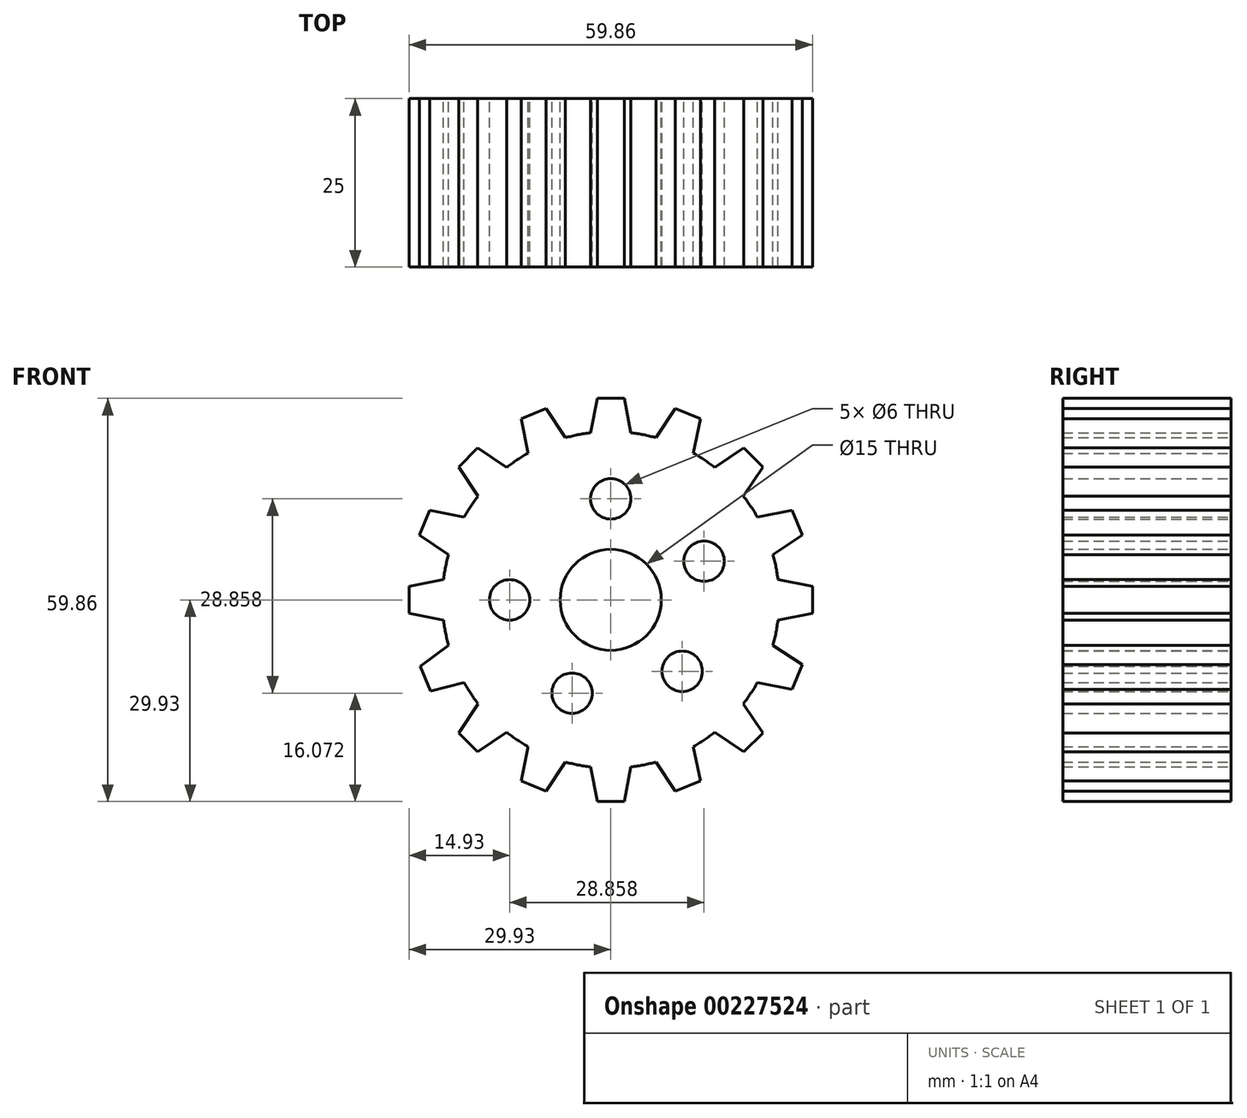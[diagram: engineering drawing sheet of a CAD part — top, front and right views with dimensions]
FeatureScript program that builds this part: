
annotation { "Feature Type Name" : "Feature", "Feature Type Description" : "" }
export const myFeature = defineFeature(function(context is Context, id is Id, definition is map)
    precondition{}
    {
        {
            var Q0;
            Q0=qCreatedBy(makeId("Front.planeOp"),FACE);
            var sketch = newSketch(context, id + "F0", { "sketchPlane" : qUnion([Q0])});
            skCircle(sketch, "E0", {"center": v(0, 0) * mm, "radius": 7.5 * mm});
            skArc(sketch, "E1", {"start": v(6.73, 24.08) * mm, "mid": v(4.88, 24.52) * mm, "end": v(3, 24.82) * mm});
            skLineSegment(sketch, "E2", {"start": v(0, 18) * mm, "end": v(0, 15) * mm, "construction": true});
            skLineSegment(sketch, "E3", {"start": v(-2, 29.93) * mm, "end": v(-3, 24.82) * mm});
            skLineSegment(sketch, "E4", {"start": v(2, 29.93) * mm, "end": v(3, 24.82) * mm});
            skLineSegment(sketch, "E5", {"start": v(-2, 29.93) * mm, "end": v(2, 29.93) * mm});
            skPoint(sketch, "E6", {"position": v(0, 29.93) * mm});
            skLineSegment(sketch, "E7.1.0", {"start": v(-13.3, 26.89) * mm, "end": v(-12.27, 21.78) * mm});
            skLineSegment(sketch, "E7.1.2", {"start": v(-9.6, 28.42) * mm, "end": v(-6.73, 24.08) * mm});
            skLineSegment(sketch, "E7.1.3", {"start": v(-13.3, 26.89) * mm, "end": v(-9.6, 28.42) * mm});
            skLineSegment(sketch, "E7.2.0", {"start": v(-22.58, 19.75) * mm, "end": v(-19.67, 15.43) * mm});
            skLineSegment(sketch, "E7.2.2", {"start": v(-19.75, 22.58) * mm, "end": v(-15.43, 19.67) * mm});
            skLineSegment(sketch, "E7.2.3", {"start": v(-22.58, 19.75) * mm, "end": v(-19.75, 22.58) * mm});
            skLineSegment(sketch, "E7.3.0", {"start": v(-28.42, 9.6) * mm, "end": v(-24.08, 6.73) * mm});
            skLineSegment(sketch, "E7.3.2", {"start": v(-26.89, 13.3) * mm, "end": v(-21.78, 12.27) * mm});
            skLineSegment(sketch, "E7.3.3", {"start": v(-28.42, 9.6) * mm, "end": v(-26.89, 13.3) * mm});
            skLineSegment(sketch, "E7.4.0", {"start": v(-29.93, -2) * mm, "end": v(-24.82, -3) * mm});
            skLineSegment(sketch, "E7.4.2", {"start": v(-29.93, 2) * mm, "end": v(-24.82, 3) * mm});
            skLineSegment(sketch, "E7.4.3", {"start": v(-29.93, -2) * mm, "end": v(-29.93, 2) * mm});
            skLineSegment(sketch, "E7.5.0", {"start": v(-26.72, -13.54) * mm, "end": v(-21.78, -12.27) * mm});
            skLineSegment(sketch, "E7.5.2", {"start": v(-28.25, -9.84) * mm, "end": v(-24.08, -6.73) * mm});
            skLineSegment(sketch, "E7.5.3", {"start": v(-26.72, -13.54) * mm, "end": v(-28.25, -9.84) * mm});
            skLineSegment(sketch, "E7.6.0", {"start": v(-19.75, -22.58) * mm, "end": v(-15.43, -19.67) * mm});
            skLineSegment(sketch, "E7.6.2", {"start": v(-22.58, -19.75) * mm, "end": v(-19.67, -15.43) * mm});
            skLineSegment(sketch, "E7.6.3", {"start": v(-19.75, -22.58) * mm, "end": v(-22.58, -19.75) * mm});
            skLineSegment(sketch, "E7.7.0", {"start": v(-9.6, -28.42) * mm, "end": v(-6.73, -24.08) * mm});
            skLineSegment(sketch, "E7.7.2", {"start": v(-13.3, -26.89) * mm, "end": v(-12.27, -21.78) * mm});
            skLineSegment(sketch, "E7.7.3", {"start": v(-9.6, -28.42) * mm, "end": v(-13.3, -26.89) * mm});
            skLineSegment(sketch, "E7.8.0", {"start": v(2, -29.93) * mm, "end": v(3, -24.82) * mm});
            skLineSegment(sketch, "E7.8.2", {"start": v(-2, -29.93) * mm, "end": v(-3, -24.82) * mm});
            skLineSegment(sketch, "E7.8.3", {"start": v(2, -29.93) * mm, "end": v(-2, -29.93) * mm});
            skLineSegment(sketch, "E7.9.0", {"start": v(13.3, -26.89) * mm, "end": v(12.27, -21.78) * mm});
            skLineSegment(sketch, "E7.9.2", {"start": v(9.6, -28.42) * mm, "end": v(6.73, -24.08) * mm});
            skLineSegment(sketch, "E7.9.3", {"start": v(13.3, -26.89) * mm, "end": v(9.6, -28.42) * mm});
            skLineSegment(sketch, "E7.10.0", {"start": v(22.58, -19.75) * mm, "end": v(19.67, -15.43) * mm});
            skLineSegment(sketch, "E7.10.2", {"start": v(19.75, -22.58) * mm, "end": v(15.43, -19.67) * mm});
            skLineSegment(sketch, "E7.10.3", {"start": v(22.58, -19.75) * mm, "end": v(19.75, -22.58) * mm});
            skLineSegment(sketch, "E7.11.0", {"start": v(28.42, -9.6) * mm, "end": v(24.08, -6.73) * mm});
            skLineSegment(sketch, "E7.11.2", {"start": v(26.89, -13.3) * mm, "end": v(21.78, -12.27) * mm});
            skLineSegment(sketch, "E7.11.3", {"start": v(28.42, -9.6) * mm, "end": v(26.89, -13.3) * mm});
            skLineSegment(sketch, "E7.12.0", {"start": v(29.93, 2) * mm, "end": v(24.82, 3) * mm});
            skLineSegment(sketch, "E7.12.2", {"start": v(29.93, -2) * mm, "end": v(24.82, -3) * mm});
            skLineSegment(sketch, "E7.12.3", {"start": v(29.93, 2) * mm, "end": v(29.93, -2) * mm});
            skLineSegment(sketch, "E7.13.0", {"start": v(26.89, 13.3) * mm, "end": v(21.78, 12.27) * mm});
            skLineSegment(sketch, "E7.13.2", {"start": v(28.42, 9.6) * mm, "end": v(24.08, 6.73) * mm});
            skLineSegment(sketch, "E7.13.3", {"start": v(26.89, 13.3) * mm, "end": v(28.42, 9.6) * mm});
            skLineSegment(sketch, "E7.14.0", {"start": v(19.75, 22.58) * mm, "end": v(15.43, 19.67) * mm});
            skLineSegment(sketch, "E7.14.2", {"start": v(22.58, 19.75) * mm, "end": v(19.67, 15.43) * mm});
            skLineSegment(sketch, "E7.14.3", {"start": v(19.75, 22.58) * mm, "end": v(22.58, 19.75) * mm});
            skLineSegment(sketch, "E7.15.0", {"start": v(9.6, 28.42) * mm, "end": v(6.73, 24.08) * mm});
            skLineSegment(sketch, "E7.15.2", {"start": v(13.3, 26.89) * mm, "end": v(12.27, 21.78) * mm});
            skLineSegment(sketch, "E7.15.3", {"start": v(9.6, 28.42) * mm, "end": v(13.3, 26.89) * mm});
            skArc(sketch, "E8.trimOffspring", {"start": v(-3, 24.82) * mm, "mid": v(-4.88, 24.52) * mm, "end": v(-6.73, 24.08) * mm});
            skArc(sketch, "E9.trimOffspring", {"start": v(-12.27, 21.78) * mm, "mid": v(-13.89, 20.79) * mm, "end": v(-15.43, 19.67) * mm});
            skArc(sketch, "E10.trimOffspring", {"start": v(-19.67, 15.43) * mm, "mid": v(-20.79, 13.89) * mm, "end": v(-21.78, 12.27) * mm});
            skArc(sketch, "E11.trimOffspring", {"start": v(-24.08, 6.73) * mm, "mid": v(-24.52, 4.88) * mm, "end": v(-24.82, 3) * mm});
            skArc(sketch, "E12.trimOffspring", {"start": v(-24.82, -3) * mm, "mid": v(-24.52, -4.88) * mm, "end": v(-24.08, -6.73) * mm});
            skArc(sketch, "E13.trimOffspring", {"start": v(-21.78, -12.27) * mm, "mid": v(-20.79, -13.89) * mm, "end": v(-19.67, -15.43) * mm});
            skArc(sketch, "E14.trimOffspring", {"start": v(-15.43, -19.67) * mm, "mid": v(-13.89, -20.79) * mm, "end": v(-12.27, -21.78) * mm});
            skArc(sketch, "E15.trimOffspring", {"start": v(-6.73, -24.08) * mm, "mid": v(-4.88, -24.52) * mm, "end": v(-3, -24.82) * mm});
            skArc(sketch, "E16.trimOffspring", {"start": v(3, -24.82) * mm, "mid": v(4.88, -24.52) * mm, "end": v(6.73, -24.08) * mm});
            skArc(sketch, "E17.trimOffspring", {"start": v(12.27, -21.78) * mm, "mid": v(13.89, -20.79) * mm, "end": v(15.43, -19.67) * mm});
            skArc(sketch, "E18.trimOffspring", {"start": v(19.67, -15.43) * mm, "mid": v(20.79, -13.89) * mm, "end": v(21.78, -12.27) * mm});
            skArc(sketch, "E19.trimOffspring", {"start": v(24.08, -6.73) * mm, "mid": v(24.52, -4.88) * mm, "end": v(24.82, -3) * mm});
            skArc(sketch, "E20.trimOffspring", {"start": v(24.82, 3) * mm, "mid": v(24.52, 4.88) * mm, "end": v(24.08, 6.73) * mm});
            skArc(sketch, "E21.trimOffspring", {"start": v(21.78, 12.27) * mm, "mid": v(20.79, 13.89) * mm, "end": v(19.67, 15.43) * mm});
            skArc(sketch, "E22.trimOffspring", {"start": v(15.43, 19.67) * mm, "mid": v(13.89, 20.79) * mm, "end": v(12.27, 21.78) * mm});
            skCircle(sketch, "E23", {"center": v(0, 15) * mm, "radius": 3 * mm});
            skCircle(sketch, "E24.1.0", {"center": v(13.86, 5.74) * mm, "radius": 3 * mm});
            skCircle(sketch, "E24.2.0", {"center": v(10.6, -10.6) * mm, "radius": 3 * mm});
            skCircle(sketch, "E24.3.0", {"center": v(-5.74, -13.86) * mm, "radius": 3 * mm});
            skCircle(sketch, "E24.4.0", {"center": v(-15, 0) * mm, "radius": 3 * mm});
            skPoint(sketch, "E25.orphan", {"position": v(0, 43.59) * mm});
            skLineSegment(sketch, "E26.trimOffspring", {"start": v(0, -29.93) * mm, "end": v(0, -41.58) * mm, "construction": true});
            skSolve(sketch);
        }
        {
            var Q0;
            Q0 = qSketchRegion(id + "F0", true);
            extrude(context, id + "F1", {"entities" : qUnion([Q0]), "depth" : 25 * mm});
        }
    });
